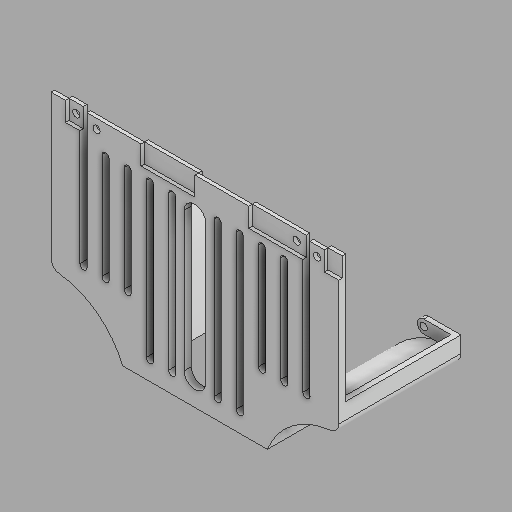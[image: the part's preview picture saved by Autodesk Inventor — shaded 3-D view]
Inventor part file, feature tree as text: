
AUTODESK INVENTOR PART (.ipt)
format: ipt  version: 2025.2 (Build 292293000, 293)  size: 385,536 bytes
history: native  units: in
note: dims shown in document units (in); Inventor stores cm internally (conversion verified against a paired STEP export)
features: sketch x9, extrude x8, fillet x2, hole x1, mirror x1
ambient origin geometry x8: Origin, YZ Plane, XZ Plane, XY Plane, X Axis, Y Axis, Z Axis, Center Point
bodies: Solid1 (feature_tree)
feature tree (21):
  extrude  "Extrusion1"  Depth=3.5in
  extrude  "Extrusion2"  Depth=0.5in
  fillet  "Fillet1"  Radius=1.75in
  fillet  "Fillet2"  Radius=0.1875in
  extrude  "Extrusion3"  Depth=0.1875in
  extrude  "Extrusion4"  TaperAngle=0.0deg  [1 undecoded]
  extrude  "Extrusion5"  Depth=0.25in
  hole  "Hole2"  [1 undecoded]
  extrude  "Extrusion6"  Depth=1.4062in
  extrude  "Extrusion7"  Depth=0.0938in TaperAngle=0.0deg
  extrude  "Extrusion8"  Depth=0.25in
  mirror  "Mirror2"
  sketch  "Sketch1"  dims[d0=3.5in d1=13.0in]
  sketch  "Sketch3"  dims[d3=2.0in d4=0.5in d5=1.75in d6=0.1875in d7=0.0in]
  sketch  "Sketch4"  dims[d22=6.0in d23=0.1875in]
  sketch  "Sketch5"  dims[d24=0.75in d25=0.0in d26=0.0in]
  sketch  "Sketch6"  dims[d27=3.0in d28=0.25in]
  sketch  "Sketch7"  dims[d29=2.0in d30=0.5in]
  sketch  "Sketch8"  dims[d31=1.0in d32=0.0in d33=1.4062in]
  sketch  "Sketch9"  dims[d34=1.4062in d35=0.0938in d36=0.0in]
  sketch  "Sketch10"  dims[d37=0.0938in d38=0.0in d39=0.25in d40=0.25in d41=0.1875in d42=0.1875in d43=0.75in d44=0.375in d45=0.25in d46=0.5635in d47=1.0in d48=0.0in d49=0.0in d50=0.0in d51=0.5in d53=0.5625in d54=0.25in d55=0.1367in d56=3.0in d57=0.0in d58=0.125in d59=3.0in d60=0.0in]
note: 2 required parameter values undecoded (feature->parameter linkage not recoverable at this tier; creation-order binding heuristic only, values carry confidence <= 0.55)
